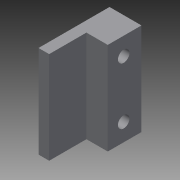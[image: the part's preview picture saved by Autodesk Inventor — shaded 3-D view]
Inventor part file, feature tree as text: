
AUTODESK INVENTOR PART (.ipt)
format: ipt  version: 2015 (Build 190159000, 159)  size: 92,672 bytes
history: native  units: mm
features: other x2, extrude x2, hole x2, sketch x2
ambient origin geometry x8: Origin, YZ Plane, XZ Plane, XY Plane, X Axis, Y Axis, Z Axis, Center Point
bodies: Body1 (feature_tree)
feature tree (8):
  other  "솔리드1"
  extrude  "돌출1"  Depth=6.0mm
  extrude  "돌출2"  Depth=26.0mm
  hole  "구멍1"  [1 undecoded]
  hole  "구멍2"  [1 undecoded]
  other  "두껍게 하기1"
  sketch  "스케치1"
  sketch  "스케치2"
note: 2 required parameter values undecoded (feature->parameter linkage not recoverable at this tier; creation-order binding heuristic only, values carry confidence <= 0.55)
